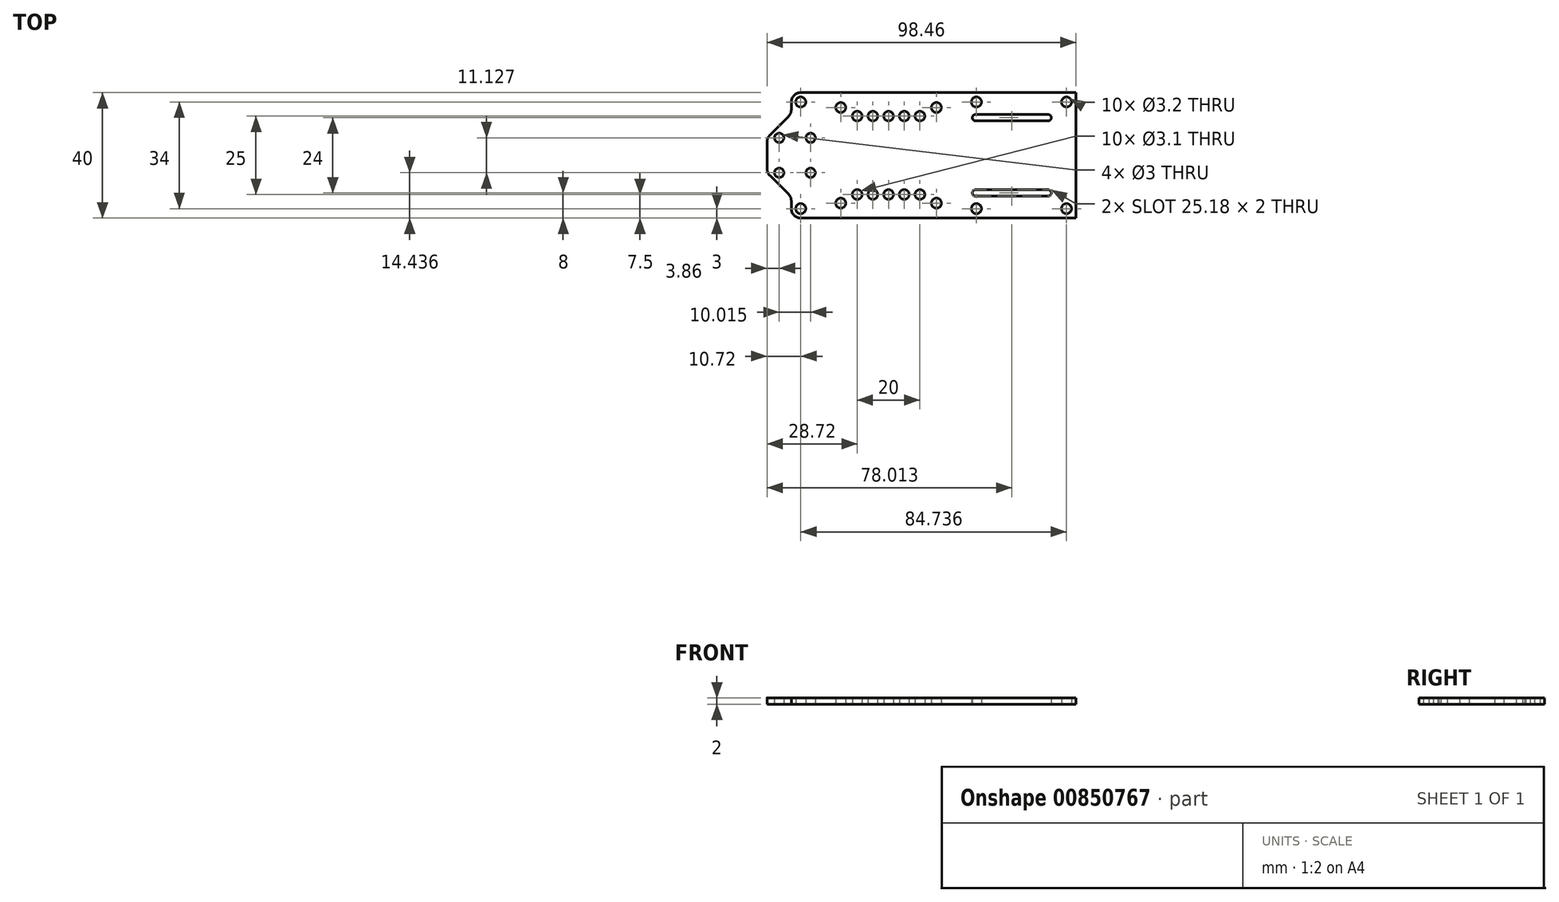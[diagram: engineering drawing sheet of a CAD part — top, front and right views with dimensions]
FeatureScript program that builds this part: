
annotation { "Feature Type Name" : "Feature", "Feature Type Description" : "" }
export const myFeature = defineFeature(function(context is Context, id is Id, definition is map)
    precondition{}
    {
        {
            var Q0;
            Q0=qCreatedBy(makeId("Top.planeOp"),FACE);
            var sketch = newSketch(context, id + "F0", { "sketchPlane" : qUnion([Q0])});
            skPoint(sketch, "E0.middle", {"position": v(0, 0) * mm});
            skLineSegment(sketch, "E1", {"start": v(14, -0.05) * mm, "end": v(-14, -0.05) * mm, "construction": true});
            skLineSegment(sketch, "E2", {"start": v(0, 0) * mm, "end": v(15.25, 0) * mm, "construction": true});
            skLineSegment(sketch, "E3", {"start": v(15.25, 0) * mm, "end": v(15.25, 15.25) * mm, "construction": true});
            skCircle(sketch, "E4", {"center": v(15.25, 15.25) * mm, "radius": 1.6 * mm});
            skCircle(sketch, "E5.MirrorC", {"center": v(-15.25, 15.25) * mm, "radius": 1.6 * mm});
            skLineSegment(sketch, "E6.MirrorCS", {"start": v(0, 0) * mm, "end": v(-15.25, 0) * mm, "construction": true});
            skCircle(sketch, "E7.MirrorC", {"center": v(-15.25, -15.25) * mm, "radius": 1.6 * mm});
            skCircle(sketch, "E8.MirrorC", {"center": v(15.25, -15.25) * mm, "radius": 1.6 * mm});
            skLineSegment(sketch, "E9.bottom", {"start": v(18.85, -18.85) * mm, "end": v(-18.85, -18.85) * mm});
            skLineSegment(sketch, "E9.top", {"start": v(18.85, 18.85) * mm, "end": v(-18.85, 18.85) * mm});
            skLineSegment(sketch, "E9.left", {"start": v(18.85, -18.85) * mm, "end": v(18.85, 18.85) * mm});
            skLineSegment(sketch, "E9.right", {"start": v(-18.85, -18.85) * mm, "end": v(-18.85, 18.85) * mm});
            skLineSegment(sketch, "E10", {"start": v(0, -20) * mm, "end": v(59.74, -20) * mm});
            skLineSegment(sketch, "E11", {"start": v(0, -20) * mm, "end": v(-31, -20) * mm});
            skLineSegment(sketch, "E12", {"start": v(0, -20) * mm, "end": v(0, 0) * mm, "construction": true});
            skLineSegment(sketch, "E13", {"start": v(59.74, -20) * mm, "end": v(59.74, 0) * mm});
            skLineSegment(sketch, "E14", {"start": v(-31, -20) * mm, "end": v(-31, -13.28) * mm});
            skLineSegment(sketch, "E15.MirrorCS", {"start": v(59.74, 20) * mm, "end": v(59.74, 0) * mm});
            skLineSegment(sketch, "E16.MirrorCS", {"start": v(-31, 20) * mm, "end": v(-31, 13.28) * mm});
            skLineSegment(sketch, "E17.MirrorCS", {"start": v(0, 20) * mm, "end": v(59.74, 20) * mm});
            skLineSegment(sketch, "E18.MirrorCS", {"start": v(0, 20) * mm, "end": v(-31, 20) * mm});
            skLineSegment(sketch, "E19", {"start": v(59.74, -20) * mm, "end": v(56.74, -17) * mm, "construction": true});
            skCircle(sketch, "E20", {"center": v(56.74, -17) * mm, "radius": 1.6 * mm});
            skCircle(sketch, "E21.MirrorC", {"center": v(56.74, 17) * mm, "radius": 1.6 * mm});
            skLineSegment(sketch, "E22", {"start": v(-31, -20) * mm, "end": v(-28, -17) * mm, "construction": true});
            skCircle(sketch, "E23", {"center": v(-28, -17) * mm, "radius": 1.6 * mm});
            skCircle(sketch, "E24.MirrorC", {"center": v(-28, 17) * mm, "radius": 1.6 * mm});
            skLineSegment(sketch, "E25", {"start": v(28, 20) * mm, "end": v(28, 17) * mm, "construction": true});
            skCircle(sketch, "E26", {"center": v(28, 17) * mm, "radius": 1.6 * mm});
            skCircle(sketch, "E27.MirrorC", {"center": v(28, -17) * mm, "radius": 1.6 * mm});
            skLineSegment(sketch, "E28", {"start": v(-31, 6) * mm, "end": v(-31, 5.56) * mm});
            skLineSegment(sketch, "E29.bottom", {"start": v(-38.72, 5.56) * mm, "end": v(-31, 5.56) * mm});
            skLineSegment(sketch, "E29.top", {"start": v(-38.72, -5.56) * mm, "end": v(-31, -5.56) * mm});
            skLineSegment(sketch, "E29.left", {"start": v(-38.72, 5.56) * mm, "end": v(-38.72, -5.56) * mm});
            skPoint(sketch, "E29.middle", {"position": v(-31, 0) * mm});
            skPoint(sketch, "E30.orphan", {"position": v(-23.28, -5.56) * mm});
            skPoint(sketch, "E31.orphan", {"position": v(-23.28, 5.56) * mm});
            skLineSegment(sketch, "E32", {"start": v(-38.72, -5.56) * mm, "end": v(-31, -13.28) * mm});
            skLineSegment(sketch, "E33", {"start": v(-38.72, 5.56) * mm, "end": v(-31, 13.28) * mm});
            skCircle(sketch, "E34", {"center": v(-34.86, -5.56) * mm, "radius": 1.5 * mm});
            skCircle(sketch, "E35", {"center": v(-34.86, 5.56) * mm, "radius": 1.5 * mm});
            skCircle(sketch, "E36", {"center": v(-24.84, -5.56) * mm, "radius": 1.5 * mm});
            skCircle(sketch, "E37", {"center": v(-24.84, 5.56) * mm, "radius": 1.5 * mm});
            skLineSegment(sketch, "E38.trimOffspring", {"start": v(-31, -6) * mm, "end": v(-31, -5.56) * mm});
            skLineSegment(sketch, "E39.trimOffspring", {"start": v(-31, -5.56) * mm, "end": v(-31, -6) * mm});
            skLineSegment(sketch, "E40", {"start": v(0, 0) * mm, "end": v(0, 12.5) * mm, "construction": true});
            skLineSegment(sketch, "E41", {"start": v(-10, 12.5) * mm, "end": v(10, 12.5) * mm, "construction": true});
            skLineSegment(sketch, "E42", {"start": v(0, 12.5) * mm, "end": v(-10, 12.5) * mm, "construction": true});
            skLineSegment(sketch, "E43", {"start": v(0, 12.5) * mm, "end": v(10, 12.5) * mm, "construction": true});
            skCircle(sketch, "E44", {"center": v(0, 12.5) * mm, "radius": 1.55 * mm});
            skCircle(sketch, "E45", {"center": v(5, 12.5) * mm, "radius": 1.55 * mm});
            skCircle(sketch, "E46", {"center": v(10, 12.5) * mm, "radius": 1.55 * mm});
            skCircle(sketch, "E47", {"center": v(-5, 12.5) * mm, "radius": 1.55 * mm});
            skCircle(sketch, "E48", {"center": v(-10, 12.5) * mm, "radius": 1.55 * mm});
            skCircle(sketch, "E49.MirrorC", {"center": v(10, -12.5) * mm, "radius": 1.55 * mm});
            skCircle(sketch, "E50.MirrorC", {"center": v(-10, -12.5) * mm, "radius": 1.55 * mm});
            skLineSegment(sketch, "E51.MirrorCS", {"start": v(-10, -12.5) * mm, "end": v(10, -12.5) * mm, "construction": true});
            skLineSegment(sketch, "E52.MirrorCS", {"start": v(0, -12.5) * mm, "end": v(10, -12.5) * mm, "construction": true});
            skLineSegment(sketch, "E53.MirrorCS", {"start": v(0, -12.5) * mm, "end": v(-10, -12.5) * mm, "construction": true});
            skCircle(sketch, "E54.MirrorC", {"center": v(-5, -12.5) * mm, "radius": 1.55 * mm});
            skCircle(sketch, "E55.MirrorC", {"center": v(0, -12.5) * mm, "radius": 1.55 * mm});
            skCircle(sketch, "E56.MirrorC", {"center": v(5, -12.5) * mm, "radius": 1.55 * mm});
            skLineSegment(sketch, "E57", {"start": v(18.85, 0) * mm, "end": v(59.74, 0) * mm, "construction": true});
            skLineSegment(sketch, "E58", {"start": v(39.3, 0) * mm, "end": v(39.3, -11) * mm, "construction": true});
            skLineSegment(sketch, "E59.bottom", {"start": v(39.3, -11) * mm, "end": v(50.88, -11) * mm});
            skLineSegment(sketch, "E59.top", {"start": v(39.3, -13) * mm, "end": v(50.88, -13) * mm});
            skLineSegment(sketch, "E59.left", {"start": v(39.3, -11) * mm, "end": v(39.3, -13) * mm});
            skLineSegment(sketch, "E59.right", {"start": v(50.88, -11) * mm, "end": v(50.88, -12) * mm});
            skLineSegment(sketch, "E60.MirrorCS", {"start": v(39.3, -13) * mm, "end": v(27.7, -13) * mm});
            skLineSegment(sketch, "E61.MirrorCS", {"start": v(27.7, -11) * mm, "end": v(27.7, -12) * mm});
            skLineSegment(sketch, "E62.MirrorCS", {"start": v(39.3, -11) * mm, "end": v(27.7, -11) * mm});
            skArc(sketch, "E63", {"start": v(50.88, -13) * mm, "mid": v(51.88, -12) * mm, "end": v(50.88, -11) * mm});
            skArc(sketch, "E64", {"start": v(27.7, -11) * mm, "mid": v(26.7, -12) * mm, "end": v(27.7, -13) * mm});
            skLineSegment(sketch, "E65.MirrorCS", {"start": v(27.7, 11) * mm, "end": v(27.7, 12) * mm});
            skLineSegment(sketch, "E66.MirrorCS", {"start": v(39.3, 11) * mm, "end": v(39.3, 13) * mm});
            skLineSegment(sketch, "E67.MirrorCS", {"start": v(50.88, 11) * mm, "end": v(50.88, 12) * mm});
            skLineSegment(sketch, "E68.MirrorCS", {"start": v(39.3, 11) * mm, "end": v(27.7, 11) * mm});
            skLineSegment(sketch, "E69.MirrorCS", {"start": v(39.3, 13) * mm, "end": v(27.7, 13) * mm});
            skLineSegment(sketch, "E70.MirrorCS", {"start": v(39.3, 11) * mm, "end": v(50.88, 11) * mm});
            skLineSegment(sketch, "E71.MirrorCS", {"start": v(39.3, 13) * mm, "end": v(50.88, 13) * mm});
            skArc(sketch, "E72.MirrorCS", {"start": v(50.88, 13) * mm, "mid": v(51.88, 12) * mm, "end": v(50.88, 11) * mm});
            skArc(sketch, "E73.MirrorCS", {"start": v(27.7, 11) * mm, "mid": v(26.7, 12) * mm, "end": v(27.7, 13) * mm});
            skSolve(sketch);
        }
        {
            var Q0;
            Q0 = qSketchRegion(id + "F0", true);
            var Q1;
            Q1=makeQuery(id+"F0.imprint","IMPRINT",FACE,{"disambiguationData":[TD([[makeQuery(id+"F0.imprint","IMPRINT",EDGE,{"derivedFrom":sQuery(id+"F0.wireOp",EDGE,"E4")}),-1.0]])]});
            extrude(context, id + "F1", {"entities" : qUnion([Q0, Q1]), "depth" : 2 * mm, "offsetDistance" : 25 * mm});
        }
        {
            var Q0;
            Q0=makeQuery(id+"F1.opExtrude","SWEPT_EDGE",EDGE,{"disambiguationData":[OSD([sQuery(id+"F0.wireOp",EDGE,"E11"),sQuery(id+"F0.wireOp",EDGE,"E14")])]});
            var Q1;
            Q1=makeQuery(id+"F1.opExtrude","SWEPT_EDGE",EDGE,{"disambiguationData":[OSD([sQuery(id+"F0.wireOp",EDGE,"E16.MirrorCS"),sQuery(id+"F0.wireOp",EDGE,"E18.MirrorCS")])]});
            var Q2;
            Q2=makeQuery(id+"F1.opExtrude","SWEPT_EDGE",EDGE,{"disambiguationData":[OSD([sQuery(id+"F0.wireOp",EDGE,"E16.MirrorCS"),sQuery(id+"F0.wireOp",EDGE,"E33")])]});
            var Q3;
            Q3=makeQuery(id+"F1.opExtrude","SWEPT_EDGE",EDGE,{"disambiguationData":[OSD([sQuery(id+"F0.wireOp",EDGE,"E29.left"),sQuery(id+"F0.wireOp",EDGE,"E33")])]});
            var Q4;
            Q4=makeQuery(id+"F1.opExtrude","SWEPT_EDGE",EDGE,{"disambiguationData":[OSD([sQuery(id+"F0.wireOp",EDGE,"E29.left"),sQuery(id+"F0.wireOp",EDGE,"E32")])]});
            var Q5;
            Q5=makeQuery(id+"F1.opExtrude","SWEPT_EDGE",EDGE,{"disambiguationData":[OSD([sQuery(id+"F0.wireOp",EDGE,"E14"),sQuery(id+"F0.wireOp",EDGE,"E32")])]});
            fillet(context, id + "F2", {"entities" : qUnion([Q0, Q1, Q2, Q3, Q4, Q5]), "radius" : 3 * mm, "tangentPropagation" : true, "allowEdgeOverflow" : false});
        }
    });
